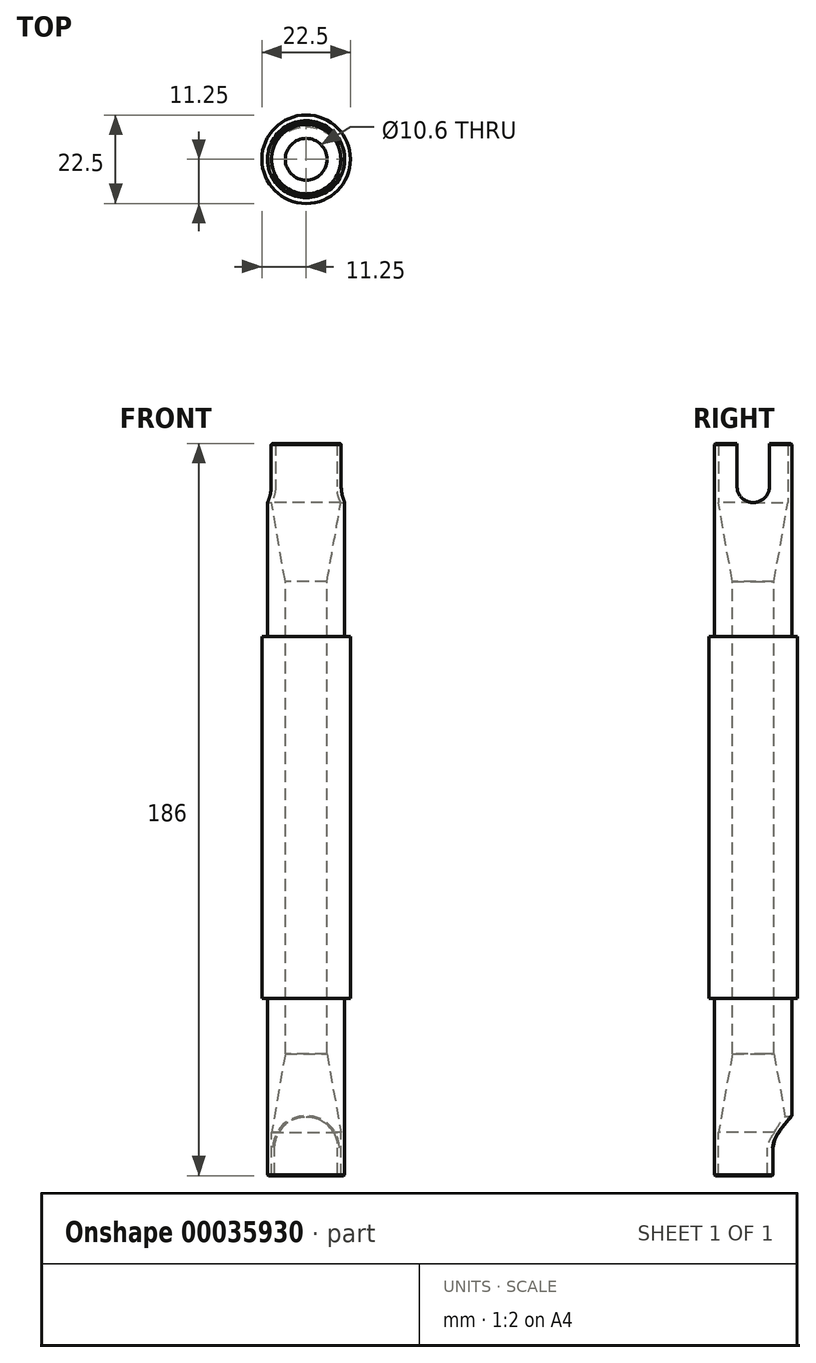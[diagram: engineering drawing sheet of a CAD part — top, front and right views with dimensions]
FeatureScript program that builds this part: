
annotation { "Feature Type Name" : "Feature", "Feature Type Description" : "" }
export const myFeature = defineFeature(function(context is Context, id is Id, definition is map)
    precondition{}
    {
        {
            var Q0;
            Q0=qCreatedBy(makeId("Top.planeOp"),FACE);
            var sketch = newSketch(context, id + "F0", { "sketchPlane" : qUnion([Q0])});
            skCircle(sketch, "E0", {"center": v(0, 0) * mm, "radius": 9.8 * mm});
            skCircle(sketch, "E1", {"center": v(0, 0) * mm, "radius": 5.3 * mm});
            skCircle(sketch, "E2", {"center": v(0, 0) * mm, "radius": 11.25 * mm});
            skSolve(sketch);
        }
        {
            var Q0;
            Q0=makeQuery(id+"F0.imprint","IMPRINT",FACE,{"disambiguationData":[TD([[makeQuery(id+"F0.imprint","IMPRINT",EDGE,{"derivedFrom":sQuery(id+"F0.wireOp",EDGE,"E0")}),-1.0]])]});
            extrude(context, id + "F1", {"entities" : qUnion([Q0]), "endBound" : BoundingType.SYMMETRIC, "depth" : 92 * mm});
        }
        {
            var Q0;
            Q0=makeQuery(id+"F0.imprint","IMPRINT",FACE,{"disambiguationData":[TD([[makeQuery(id+"F0.imprint","IMPRINT",EDGE,{"derivedFrom":sQuery(id+"F0.wireOp",EDGE,"E0")}),1.0]])]});
            extrude(context, id + "F2", {"entities" : qUnion([Q0]), "operationType" : NewBodyOperationType.ADD, "endBound" : BoundingType.SYMMETRIC, "oppositeDirection" : true, "depth" : 160 * mm});
        }
        {
            var Q0;
            Q0=makeQuery(id+"F2.opExtrude","CAP_EDGE",EDGE,{"disambiguationData":[OSD([sQuery(id+"F0.wireOp",EDGE,"E1")])],"isStart":true});
            chamfer(context, id + "F3", {"entities" : qUnion([Q0]), "chamferType" : ChamferType.TWO_OFFSETS, "width1" : 3.5 * mm, "oppositeDirection" : true, "width2" : 20 * mm, "tangentPropagation" : true});
        }
        {
            var Q0;
            Q0=makeQuery(id+"F2.opExtrude","CAP_EDGE",EDGE,{"disambiguationData":[OSD([sQuery(id+"F0.wireOp",EDGE,"E1")])],"isStart":false});
            chamfer(context, id + "F4", {"entities" : qUnion([Q0]), "chamferType" : ChamferType.TWO_OFFSETS, "width1" : 3.5 * mm, "oppositeDirection" : false, "width2" : 20 * mm, "tangentPropagation" : true});
        }
        {
            var Q0;
            Q0=qCreatedBy(makeId("Front.planeOp"),FACE);
            var sketch = newSketch(context, id + "F5", { "sketchPlane" : qUnion([Q0])});
            skCircle(sketch, "E3", {"center": v(0, -84) * mm, "radius": 8 * mm});
            skLineSegment(sketch, "E4", {"start": v(0, -84) * mm, "end": v(-8, -84) * mm});
            skLineSegment(sketch, "E5", {"start": v(-8, -84) * mm, "end": v(-8, -104.47) * mm});
            skLineSegment(sketch, "E6", {"start": v(0, -84) * mm, "end": v(8, -84) * mm});
            skLineSegment(sketch, "E7", {"start": v(8, -84) * mm, "end": v(8, -104.47) * mm});
            skLineSegment(sketch, "E8", {"start": v(8, -104.47) * mm, "end": v(-8, -104.47) * mm});
            skSolve(sketch);
        }
        {
            var Q0;
            Q0=makeQuery(id+"F2.opExtrude","CAP_FACE",FACE,{"disambiguationData":[OSD([sQuery(id+"F0.wireOp",EDGE,"E0"),sQuery(id+"F0.wireOp",EDGE,"E1")])],"isStart":false});
            extrude(context, id + "F6", {"entities" : qUnion([Q0]), "operationType" : NewBodyOperationType.ADD, "depth" : 11 * mm});
        }
        {
            var Q0;
            {var subQ1=sQuery(id+"F5.wireOp",EDGE,"E4");Q0=makeQuery(id+"F5.imprint","IMPRINT",FACE,{"disambiguationData":[TD([[makeQuery(id+"F5.imprint","IMPRINT",EDGE,{"derivedFrom":subQ1}),-1.0]])]});}
            var Q1;
            {var subQ1=sQuery(id+"F5.wireOp",EDGE,"E4");Q1=makeQuery(id+"F5.imprint","IMPRINT",FACE,{"disambiguationData":[TD([[makeQuery(id+"F5.imprint","IMPRINT",EDGE,{"derivedFrom":subQ1}),1.0]])]});}
            var Q2;
            {var subQ1=sQuery(id+"F5.wireOp",EDGE,"E5");Q2=makeQuery(id+"F5.imprint","IMPRINT",FACE,{"disambiguationData":[TD([[makeQuery(id+"F5.imprint","IMPRINT",EDGE,{"derivedFrom":subQ1}),1.0]])]});}
            extrude(context, id + "F7", {"entities" : qUnion([Q0, Q1, Q2]), "operationType" : NewBodyOperationType.REMOVE, "oppositeDirection" : true, "depth" : 25 * mm});
        }
        {
            var Q0;
            Q0=makeQuery(id+"F2.opExtrude","CAP_FACE",FACE,{"disambiguationData":[OSD([sQuery(id+"F0.wireOp",EDGE,"E0"),sQuery(id+"F0.wireOp",EDGE,"E1")])],"isStart":true});
            extrude(context, id + "F8", {"entities" : qUnion([Q0]), "operationType" : NewBodyOperationType.ADD, "depth" : 15 * mm});
        }
        {
            var Q0;
            {var subQ0=sQuery(id+"F0.wireOp",EDGE,"E0");Q0=makeQuery(id+"F7.boolean.opBoolean","INTERSECT",EDGE,{"derivedFrom":[makeQuery(id+"F6.boolean.opBoolean","MERGE",FACE,{"derivedFrom":[makeQuery(id+"F2.boolean.opBoolean","SPLIT",FACE,{"disambiguationData":[TD([makeQuery(id+"F1.opExtrude","CAP_FACE",FACE,{"disambiguationData":[OSD([subQ0,sQuery(id+"F0.wireOp",EDGE,"E2")])],"isStart":true})])],"derivedFrom":makeQuery(id+"F2.opExtrude","SWEPT_FACE",FACE,{"disambiguationData":[OSD([subQ0])]})}),makeQuery(id+"F6.opExtrude","SWEPT_FACE",FACE,{"disambiguationData":[OSD([subQ0])]})]}),makeQuery(id+"F7.opExtrude","SWEPT_FACE",FACE,{"disambiguationData":[OSD([sQuery(id+"F5.wireOp",EDGE,"E3")])]})]});}
            fillet(context, id + "F9", {"entities" : qUnion([Q0]), "radius" : .25 * mm, "tangentPropagation" : true, "allowEdgeOverflow" : false});
        }
        {
            var Q0;
            Q0=makeQuery(id+"F6.opExtrude","CAP_EDGE",EDGE,{"disambiguationData":[OSD([sQuery(id+"F0.wireOp",EDGE,"E0")])],"isStart":false});
            var Q1;
            Q1=makeQuery(id+"F8.opExtrude","CAP_EDGE",EDGE,{"disambiguationData":[OSD([sQuery(id+"F0.wireOp",EDGE,"E0")])],"isStart":false});
            chamfer(context, id + "F10", {"entities" : qUnion([Q0, Q1]), "width" : .25 * mm, "tangentPropagation" : true});
        }
        {
            var Q0;
            Q0=makeQuery(id+"F1.opExtrude","CAP_EDGE",EDGE,{"disambiguationData":[OSD([sQuery(id+"F0.wireOp",EDGE,"E0")])],"isStart":false});
            var Q1;
            Q1=makeQuery(id+"F1.opExtrude","CAP_EDGE",EDGE,{"disambiguationData":[OSD([sQuery(id+"F0.wireOp",EDGE,"E0")])],"isStart":true});
            fillet(context, id + "F11", {"entities" : qUnion([Q0, Q1]), "radius" : .25 * mm, "tangentPropagation" : true, "allowEdgeOverflow" : false});
        }
        {
            var Q0;
            Q0=qCreatedBy(makeId("Right.planeOp"),FACE);
            var sketch = newSketch(context, id + "F12", { "sketchPlane" : qUnion([Q0])});
            skLineSegment(sketch, "E9.rect.bottom", {"start": v(4.1, 80) * mm, "end": v(-4.1, 80) * mm});
            skLineSegment(sketch, "E9.rect.top", {"start": v(4.1, 110) * mm, "end": v(-4.1, 110) * mm});
            skLineSegment(sketch, "E9.rect.left", {"start": v(4.1, 80) * mm, "end": v(4.1, 110) * mm});
            skLineSegment(sketch, "E9.rect.right", {"start": v(-4.1, 80) * mm, "end": v(-4.1, 110) * mm});
            skPoint(sketch, "E9.rect.middle", {"position": v(0, 95) * mm});
            skCircle(sketch, "E10", {"center": v(0, 84.1) * mm, "radius": 4.1 * mm});
            skSolve(sketch);
        }
        {
            var Q0;
            {var subQ0=sQuery(id+"F12.wireOp",EDGE,"E10");var subQ1=makeQuery(id+"F12.imprint","INTERSECT",VERTEX,{"derivedFrom":[sQuery(id+"F12.wireOp",EDGE,"E9.rect.left"),subQ0]});Q0=makeQuery(id+"F12.imprint","IMPRINT",FACE,{"disambiguationData":[TD([[makeQuery(id+"F12.imprint","IMPRINT",EDGE,{"disambiguationData":[TD([[subQ1,-1.0]])],"derivedFrom":subQ0}),1.0]])]});}
            var Q1;
            {var subQ0=sQuery(id+"F12.wireOp",EDGE,"E9.rect.top");Q1=makeQuery(id+"F12.imprint","IMPRINT",FACE,{"disambiguationData":[TD([[makeQuery(id+"F12.imprint","IMPRINT",EDGE,{"derivedFrom":subQ0}),1.0]])]});}
            extrude(context, id + "F13", {"entities" : qUnion([Q0, Q1]), "operationType" : NewBodyOperationType.REMOVE, "endBound" : BoundingType.SYMMETRIC, "oppositeDirection" : true, "depth" : 50 * mm});
        }
    });
